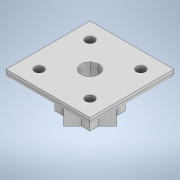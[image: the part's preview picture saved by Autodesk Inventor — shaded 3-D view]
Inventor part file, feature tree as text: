
AUTODESK INVENTOR PART (.ipt)
format: ipt  version: 2021 (Build 250183000, 183)  size: 160,768 bytes
history: native  units: mm
features: extrude x4, sketch x4, other x1, fillet x1
ambient origin geometry x8: Origin, YZ Plane, XZ Plane, XY Plane, X Axis, Y Axis, Z Axis, Center Point
bodies: Body1 (feature_tree)
feature tree (10):
  other  "Sólido1"
  extrude  "Extrusión1"  Depth=9.0mm TaperAngle=0.0deg
  extrude  "Extrusión2"  Depth=4.5mm
  extrude  "Extrusión5"  Depth=3.0mm TaperAngle=360.0deg
  fillet  "Empalme1"  Radius=6.0mm
  extrude  "Extrusión6"  Depth=2.0mm
  sketch  "Boceto1"  dims[d11=2.95mm d16=9.0mm d17=0.0mm]
  sketch  "Boceto2"  dims[d22=3.0mm d23=0.0mm d26=4.5mm]
  sketch  "Boceto5"  dims[d28=3.0mm d29=40.0mm d31=360.0deg d48=6.0mm]
  sketch  "Boceto6"  dims[d50=100.0mm d51=0.0mm d52=2.0mm d66=40.0mm d68=360.0deg d70=100.0mm d71=0.0mm d18=0.5mm d19=0.872665mm]
